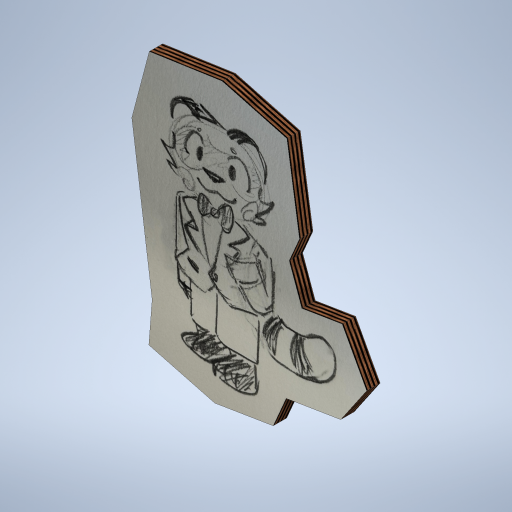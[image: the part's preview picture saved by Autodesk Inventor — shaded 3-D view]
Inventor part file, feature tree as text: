
AUTODESK INVENTOR PART (.ipt)
format: ipt  version: 2023 (Build 270158000, 158)  size: 1,283,584 bytes
history: native  units: in
note: dims shown in document units (in); Inventor stores cm internally (conversion verified against a paired STEP export)
features: extrude x1, sketch x1, other x1
ambient origin geometry x8: Origin, YZ Plane, XZ Plane, XY Plane, X Axis, Y Axis, Z Axis, Center Point
bodies: Solid1 (feature_tree)
feature tree (3):
  extrude  "Extrusion1"  Depth=1.0in
  sketch  "Sketch1"  dims[d13=1.0in d14=0.0in d15=21.0145in d18=17.4523in]
  other  "Image1"
